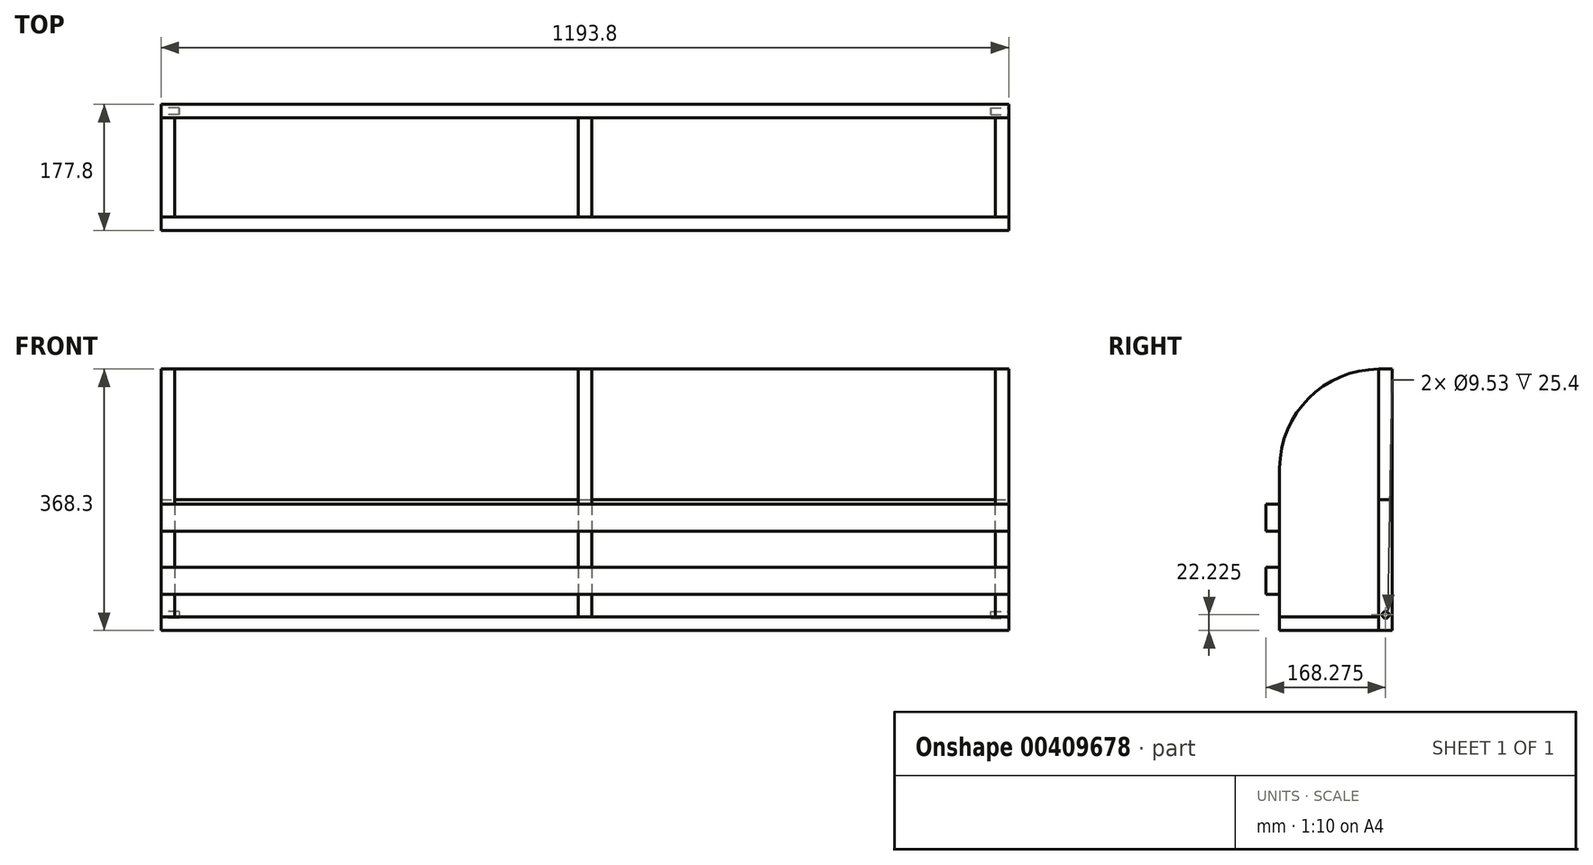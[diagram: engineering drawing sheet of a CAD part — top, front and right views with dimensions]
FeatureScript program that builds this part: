
annotation { "Feature Type Name" : "Feature", "Feature Type Description" : "" }
export const myFeature = defineFeature(function(context is Context, id is Id, definition is map)
    precondition{}
    {
        {
            var Q0;
            Q0=qCreatedBy(makeId("Front.planeOp"),FACE);
            var sketch = newSketch(context, id + "F0", { "sketchPlane" : qUnion([Q0])});
            skLineSegment(sketch, "E0.bottom", {"start": v(0, 0) * mm, "end": v(1193.8, 0) * mm});
            skLineSegment(sketch, "E0.top", {"start": v(0, 184.15) * mm, "end": v(1193.8, 184.15) * mm});
            skLineSegment(sketch, "E0.left", {"start": v(0, 0) * mm, "end": v(0, 184.15) * mm});
            skLineSegment(sketch, "E0.right", {"start": v(1193.8, 0) * mm, "end": v(1193.8, 184.15) * mm});
            skSolve(sketch);
        }
        {
            var Q0;
            Q0=makeQuery(id+"F0.imprint","IMPRINT",FACE,{"disambiguationData":[TD([[makeQuery(id+"F0.imprint","IMPRINT",EDGE,{"derivedFrom":sQuery(id+"F0.wireOp",EDGE,"E0.bottom")}),1.0]])]});
            extrude(context, id + "F1", {"entities" : qUnion([Q0]), "depth" : 19.05 * mm});
        }
        {
            var Q0;
            Q0=qCreatedBy(makeId("Front.planeOp"),FACE);
            var sketch = newSketch(context, id + "F2", { "sketchPlane" : qUnion([Q0])});
            skLineSegment(sketch, "E1.bottom", {"start": v(0, 184.15) * mm, "end": v(1193.8, 184.15) * mm});
            skLineSegment(sketch, "E1.top", {"start": v(0, 368.3) * mm, "end": v(1193.8, 368.3) * mm});
            skLineSegment(sketch, "E1.left", {"start": v(0, 184.15) * mm, "end": v(0, 368.3) * mm});
            skLineSegment(sketch, "E1.right", {"start": v(1193.8, 184.15) * mm, "end": v(1193.8, 368.3) * mm});
            skSolve(sketch);
        }
        {
            var Q0;
            Q0 = qSketchRegion(id + "F2", true);
            extrude(context, id + "F3", {"entities" : qUnion([Q0]), "depth" : 19.05 * mm});
        }
        {
            var Q0;
            Q0=qCreatedBy(makeId("Top.planeOp"),FACE);
            var sketch = newSketch(context, id + "F4", { "sketchPlane" : qUnion([Q0])});
            skLineSegment(sketch, "E2.bottom", {"start": v(0, -158.75) * mm, "end": v(1193.8, -158.75) * mm});
            skLineSegment(sketch, "E2.top", {"start": v(0, -19.05) * mm, "end": v(1193.8, -19.05) * mm});
            skLineSegment(sketch, "E2.left", {"start": v(0, -158.75) * mm, "end": v(0, -19.05) * mm});
            skLineSegment(sketch, "E2.right", {"start": v(1193.8, -158.75) * mm, "end": v(1193.8, -19.05) * mm});
            skSolve(sketch);
        }
        {
            var Q0;
            Q0=makeQuery(id+"F4.imprint","IMPRINT",FACE,{"disambiguationData":[TD([[makeQuery(id+"F4.imprint","IMPRINT",EDGE,{"derivedFrom":sQuery(id+"F4.wireOp",EDGE,"E2.bottom")}),1.0]])]});
            extrude(context, id + "F5", {"entities" : qUnion([Q0]), "depth" : 19.05 * mm});
        }
        {
            var Q0;
            Q0=makeQuery(id+"F5.opExtrude","SWEPT_FACE",FACE,{"disambiguationData":[OSD([sQuery(id+"F4.wireOp",EDGE,"E2.left")])]});
            var sketch = newSketch(context, id + "F6", { "sketchPlane" : qUnion([Q0])});
            skLineSegment(sketch, "E3.top", {"start": v(19.05, 19.05) * mm, "end": v(158.75, 19.05) * mm});
            skLineSegment(sketch, "E3.left", {"start": v(19.05, 368.3) * mm, "end": v(19.05, 19.05) * mm});
            skLineSegment(sketch, "E3.right", {"start": v(158.75, 228.6) * mm, "end": v(158.75, 19.05) * mm});
            skArc(sketch, "E4", {"start": v(158.75, 228.6) * mm, "mid": v(117.83, 327.38) * mm, "end": v(19.05, 368.3) * mm});
            skSolve(sketch);
        }
        {
            var Q0;
            Q0=makeQuery(id+"F6.imprint","IMPRINT",FACE,{"disambiguationData":[TD([[makeQuery(id+"F6.imprint","IMPRINT",EDGE,{"derivedFrom":sQuery(id+"F6.wireOp",EDGE,"E3.top")}),-1.0]])]});
            extrude(context, id + "F7", {"entities" : qUnion([Q0]), "oppositeDirection" : true, "depth" : 19.05 * mm});
        }
        {
            var Q0;
            Q0=makeQuery(id+"F5.opExtrude","SWEPT_FACE",FACE,{"disambiguationData":[OSD([sQuery(id+"F4.wireOp",EDGE,"E2.right")])]});
            var sketch = newSketch(context, id + "F8", { "sketchPlane" : qUnion([Q0])});
            skLineSegment(sketch, "E5.bottom", {"start": v(-158.75, 19.05) * mm, "end": v(-19.05, 19.05) * mm});
            skLineSegment(sketch, "E5.left", {"start": v(-158.75, 19.05) * mm, "end": v(-158.75, 228.6) * mm});
            skLineSegment(sketch, "E5.right", {"start": v(-19.05, 19.05) * mm, "end": v(-19.05, 368.3) * mm});
            skArc(sketch, "E6", {"start": v(-19.05, 368.3) * mm, "mid": v(-117.83, 327.38) * mm, "end": v(-158.75, 228.6) * mm});
            skSolve(sketch);
        }
        {
            var Q0;
            Q0=makeQuery(id+"F8.imprint","IMPRINT",FACE,{"disambiguationData":[TD([[makeQuery(id+"F8.imprint","IMPRINT",EDGE,{"derivedFrom":sQuery(id+"F8.wireOp",EDGE,"E5.bottom")}),1.0]])]});
            extrude(context, id + "F9", {"entities" : qUnion([Q0]), "oppositeDirection" : true, "depth" : 19.05 * mm});
        }
        {
            var Q0;
            Q0=makeQuery(id+"F1.opExtrude","CAP_EDGE",EDGE,{"disambiguationData":[OSD([sQuery(id+"F0.wireOp",EDGE,"E0.bottom")])],"isStart":true});
            cPoint(context, id + "F10", {"entities" : qUnion([Q0]), "parameter" : 0.5});
        }
        {
            var Q0;
            Q0=qCreatedBy(makeId("Right.planeOp"),FACE);
            var Q1;
            Q1 = qCreatedBy(id + "F10" ,VERTEX);
            cPlane(context, id + "F11", {"entities" : qUnion([Q0, Q1]), "cplaneType" : CPlaneType.PLANE_POINT, "offset" : 25.4 * mm, "width" : 152.4 * mm, "height" : 152.4 * mm});
        }
        {
            var Q0;
            Q0=qCreatedBy(id+"F11.planeOp",FACE);
            var sketch = newSketch(context, id + "F12", { "sketchPlane" : qUnion([Q0])});
            skLineSegment(sketch, "E7.top", {"start": v(-19.05, 19.05) * mm, "end": v(-158.75, 19.05) * mm});
            skLineSegment(sketch, "E7.left", {"start": v(-19.05, 368.3) * mm, "end": v(-19.05, 19.05) * mm});
            skLineSegment(sketch, "E7.right", {"start": v(-158.75, 228.6) * mm, "end": v(-158.75, 19.05) * mm});
            skArc(sketch, "E8", {"start": v(-19.05, 368.3) * mm, "mid": v(-117.83, 327.38) * mm, "end": v(-158.75, 228.6) * mm});
            skSolve(sketch);
        }
        {
            var Q0;
            Q0=makeQuery(id+"F12.imprint","IMPRINT",FACE,{"disambiguationData":[TD([[makeQuery(id+"F12.imprint","IMPRINT",EDGE,{"derivedFrom":sQuery(id+"F12.wireOp",EDGE,"E7.top")}),-1.0]])]});
            extrude(context, id + "F13", {"entities" : qUnion([Q0]), "depth" : 19.05 * mm, "symmetric" : true});
        }
        {
            var Q0;
            Q0=makeQuery(id+"F7.opExtrude","CAP_FACE",FACE,{"disambiguationData":[OSD([sQuery(id+"F6.wireOp",EDGE,"E3.top"),sQuery(id+"F6.wireOp",EDGE,"E3.left"),sQuery(id+"F6.wireOp",EDGE,"E3.right"),sQuery(id+"F6.wireOp",EDGE,"E4")])],"isStart":true});
            var sketch = newSketch(context, id + "F14", { "sketchPlane" : qUnion([Q0])});
            skLineSegment(sketch, "E9.bottom", {"start": v(158.75, 88.9) * mm, "end": v(177.8, 88.9) * mm});
            skLineSegment(sketch, "E9.top", {"start": v(158.75, 50.8) * mm, "end": v(177.8, 50.8) * mm});
            skLineSegment(sketch, "E9.left", {"start": v(158.75, 88.9) * mm, "end": v(158.75, 50.8) * mm});
            skLineSegment(sketch, "E9.right", {"start": v(177.8, 88.9) * mm, "end": v(177.8, 50.8) * mm});
            skSolve(sketch);
        }
        {
            var Q0;
            Q0=makeQuery(id+"F14.imprint","IMPRINT",FACE,{"disambiguationData":[TD([[makeQuery(id+"F14.imprint","IMPRINT",EDGE,{"derivedFrom":sQuery(id+"F14.wireOp",EDGE,"E9.bottom")}),-1.0]])]});
            var Q1;
            Q1=makeQuery(id+"F9.opExtrude","CAP_FACE",FACE,{"disambiguationData":[OSD([sQuery(id+"F8.wireOp",EDGE,"E5.bottom"),sQuery(id+"F8.wireOp",EDGE,"E5.left"),sQuery(id+"F8.wireOp",EDGE,"E5.right"),sQuery(id+"F8.wireOp",EDGE,"E6")])],"isStart":true});
            extrude(context, id + "F15", {"entities" : qUnion([Q0]), "endBound" : BoundingType.UP_TO_SURFACE, "oppositeDirection" : true, "endBoundEntityFace" : qUnion([Q1]), "depth" : 25.4 * mm});
        }
        {
            var Q0;
            Q0=makeQuery(id+"F7.opExtrude","CAP_FACE",FACE,{"disambiguationData":[OSD([sQuery(id+"F6.wireOp",EDGE,"E3.top"),sQuery(id+"F6.wireOp",EDGE,"E3.left"),sQuery(id+"F6.wireOp",EDGE,"E3.right"),sQuery(id+"F6.wireOp",EDGE,"E4")])],"isStart":true});
            var sketch = newSketch(context, id + "F16", { "sketchPlane" : qUnion([Q0])});
            skLineSegment(sketch, "E10.bottom", {"start": v(158.75, 177.8) * mm, "end": v(177.8, 177.8) * mm});
            skLineSegment(sketch, "E10.top", {"start": v(158.75, 139.7) * mm, "end": v(177.8, 139.7) * mm});
            skLineSegment(sketch, "E10.left", {"start": v(158.75, 177.8) * mm, "end": v(158.75, 139.7) * mm});
            skLineSegment(sketch, "E10.right", {"start": v(177.8, 177.8) * mm, "end": v(177.8, 139.7) * mm});
            skSolve(sketch);
        }
        {
            var Q0;
            Q0=makeQuery(id+"F16.imprint","IMPRINT",FACE,{"disambiguationData":[TD([[makeQuery(id+"F16.imprint","IMPRINT",EDGE,{"derivedFrom":sQuery(id+"F16.wireOp",EDGE,"E10.bottom")}),-1.0]])]});
            var Q1;
            Q1=makeQuery(id+"F9.opExtrude","CAP_FACE",FACE,{"disambiguationData":[OSD([sQuery(id+"F8.wireOp",EDGE,"E5.bottom"),sQuery(id+"F8.wireOp",EDGE,"E5.left"),sQuery(id+"F8.wireOp",EDGE,"E5.right"),sQuery(id+"F8.wireOp",EDGE,"E6")])],"isStart":true});
            extrude(context, id + "F17", {"entities" : qUnion([Q0]), "endBound" : BoundingType.UP_TO_SURFACE, "oppositeDirection" : true, "endBoundEntityFace" : qUnion([Q1]), "depth" : 25.4 * mm});
        }
        {
            var Q0;
            Q0=makeQuery(id+"F1.opExtrude","SWEPT_FACE",FACE,{"disambiguationData":[OSD([sQuery(id+"F0.wireOp",EDGE,"E0.right")])]});
            var sketch = newSketch(context, id + "F18", { "sketchPlane" : qUnion([Q0])});
            skCircle(sketch, "E11", {"center": v(-9.53, 22.23) * mm, "radius": 4.76 * mm});
            skPoint(sketch, "E12", {"position": v(-9.53, 0) * mm});
            skSolve(sketch);
        }
        {
            var Q0;
            Q0=makeQuery(id+"F18.imprint","IMPRINT",FACE,{"disambiguationData":[TD([[makeQuery(id+"F18.imprint","IMPRINT",EDGE,{"derivedFrom":sQuery(id+"F18.wireOp",EDGE,"E11")}),1.0]])]});
            extrude(context, id + "F19", {"entities" : qUnion([Q0]), "operationType" : NewBodyOperationType.REMOVE, "oppositeDirection" : true, "depth" : 25.4 * mm});
        }
        {
            var Q0;
            Q0=makeQuery(id+"F1.opExtrude","SWEPT_FACE",FACE,{"disambiguationData":[OSD([sQuery(id+"F0.wireOp",EDGE,"E0.left")])]});
            var sketch = newSketch(context, id + "F20", { "sketchPlane" : qUnion([Q0])});
            skCircle(sketch, "E13", {"center": v(9.53, 22.23) * mm, "radius": 4.76 * mm});
            skPoint(sketch, "E14", {"position": v(9.53, 0) * mm});
            skSolve(sketch);
        }
        {
            var Q0;
            Q0=makeQuery(id+"F20.imprint","IMPRINT",FACE,{"disambiguationData":[TD([[makeQuery(id+"F20.imprint","IMPRINT",EDGE,{"derivedFrom":sQuery(id+"F20.wireOp",EDGE,"E13")}),1.0]])]});
            extrude(context, id + "F21", {"entities" : qUnion([Q0]), "operationType" : NewBodyOperationType.REMOVE, "oppositeDirection" : true, "depth" : 25.4 * mm});
        }
    });
